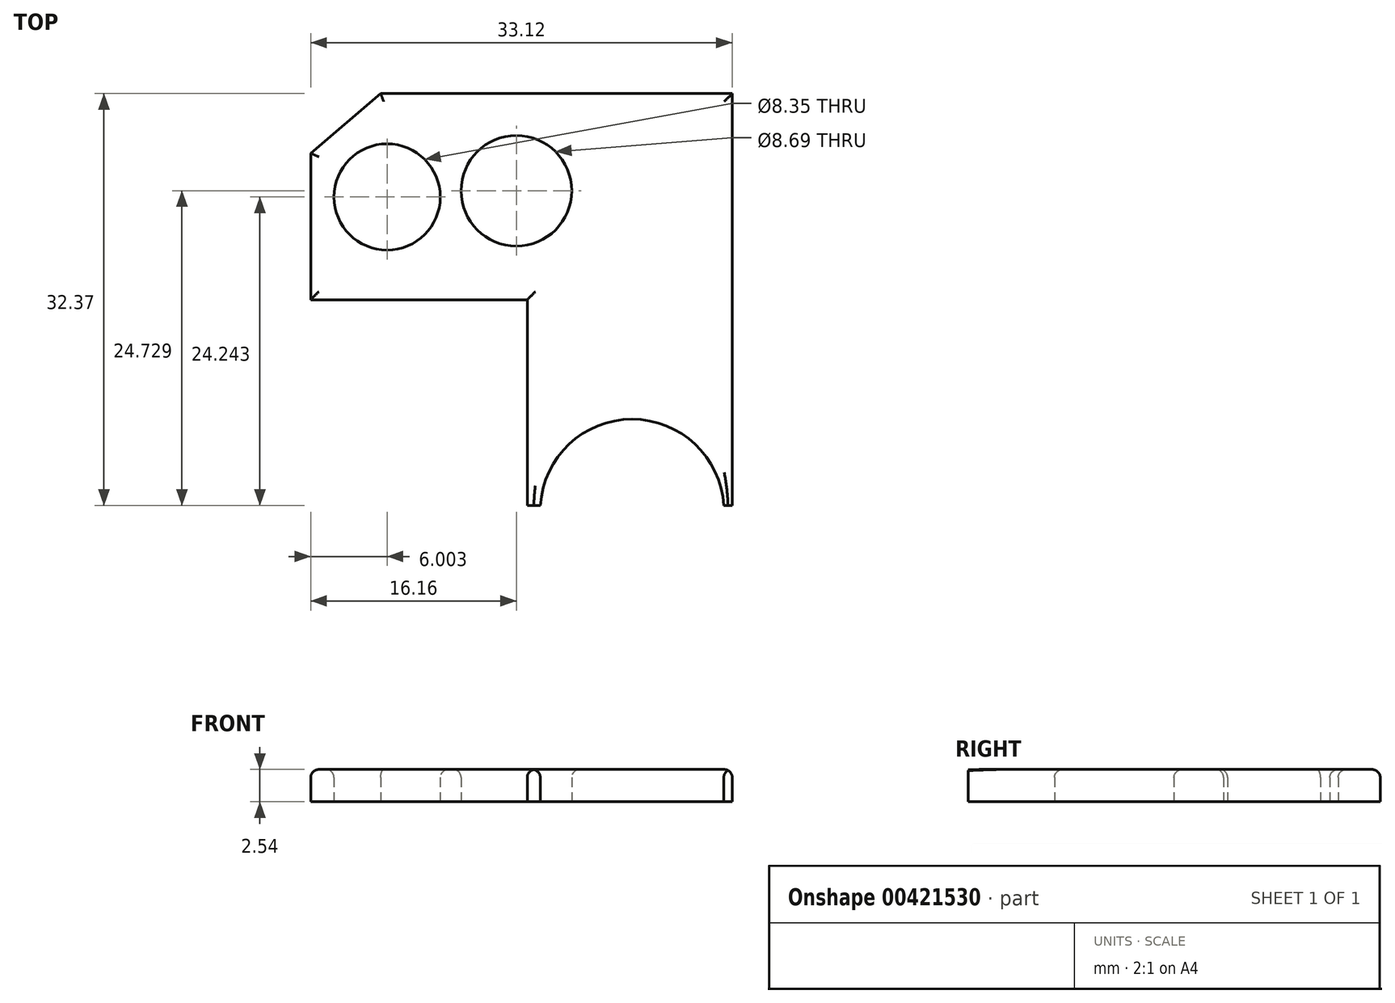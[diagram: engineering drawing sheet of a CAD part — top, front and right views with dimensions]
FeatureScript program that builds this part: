
annotation { "Feature Type Name" : "Feature", "Feature Type Description" : "" }
export const myFeature = defineFeature(function(context is Context, id is Id, definition is map)
    precondition{}
    {
        {
            var Q0;
            Q0=qCreatedBy(makeId("Top.planeOp"),FACE);
            var sketch = newSketch(context, id + "F0", { "sketchPlane" : qUnion([Q0])});
            skLineSegment(sketch, "E0", {"start": v(-16.16, 0) * mm, "end": v(-16.16, 7.98) * mm});
            skLineSegment(sketch, "E1", {"start": v(-16.16, 7.98) * mm, "end": v(-10.66, 12.67) * mm});
            skLineSegment(sketch, "E2", {"start": v(-10.66, 12.67) * mm, "end": v(16.96, 12.67) * mm});
            skLineSegment(sketch, "E3", {"start": v(16.96, 12.67) * mm, "end": v(16.96, 0) * mm});
            skLineSegment(sketch, "E4", {"start": v(16.96, 0) * mm, "end": v(16.96, -7) * mm});
            skLineSegment(sketch, "E5", {"start": v(16.96, -7) * mm, "end": v(0.86, -7) * mm});
            skLineSegment(sketch, "E6", {"start": v(0.86, -7) * mm, "end": v(0.86, -3.53) * mm});
            skLineSegment(sketch, "E7", {"start": v(0.86, -3.53) * mm, "end": v(-16.16, -3.53) * mm});
            skLineSegment(sketch, "E8", {"start": v(-16.16, -3.53) * mm, "end": v(-16.16, 0) * mm});
            skCircle(sketch, "E9", {"center": v(-10.16, 4.54) * mm, "radius": 4.18 * mm});
            skCircle(sketch, "E10", {"center": v(0, 5.03) * mm, "radius": 4.35 * mm});
            skSolve(sketch);
        }
        {
            var Q0;
            Q0=makeQuery(id+"F0.imprint","IMPRINT",FACE,{"disambiguationData":[TD([[makeQuery(id+"F0.imprint","IMPRINT",EDGE,{"derivedFrom":sQuery(id+"F0.wireOp",EDGE,"E0")}),-1.0]])]});
            extrude(context, id + "F1", {"entities" : qUnion([Q0]), "depth" : 2.54 * mm});
        }
        {
            var Q0;
            Q0=makeQuery(id+"F1.opExtrude","SWEPT_FACE",FACE,{"disambiguationData":[OSD([sQuery(id+"F0.wireOp",EDGE,"E5")])]});
            extrude(context, id + "F2", {"entities" : qUnion([Q0]), "operationType" : NewBodyOperationType.ADD, "depth" : 12.7 * mm});
        }
        {
            var Q0;
            Q0=qCreatedBy(makeId("Top.planeOp"),FACE);
            var sketch = newSketch(context, id + "F3", { "sketchPlane" : qUnion([Q0])});
            skCircle(sketch, "E11", {"center": v(6.55, -27.76) * mm, "radius": 7.22 * mm});
            skSolve(sketch);
        }
        {
            var Q0;
            Q0=makeQuery(id+"F3.imprint","IMPRINT",FACE,{"disambiguationData":[TD([[makeQuery(id+"F3.imprint","IMPRINT",EDGE,{"derivedFrom":sQuery(id+"F3.wireOp",EDGE,"E11")}),1.0]])]});
            extrude(context, id + "F4", {"entities" : qUnion([Q0]), "depth" : 12.7 * mm});
        }
        {
            var Q0;
            Q0=makeQuery(id+"F4.opExtrude","SWEPT_BODY",BODY,{"disambiguationData":[OSD([sQuery(id+"F3.wireOp",EDGE,"E11")])]});
            transform(context, id + "F5", {"entities" : qUnion([Q0]), "transformType" : TransformType.TRANSLATION_3D, "dx" : 2.54 * mm, "dy" : 7.62 * mm, "dz" : 0 * mm, "makeCopy" : false});
        }
        {
            var Q0;
            Q0=makeQuery(id+"F4.opExtrude","SWEPT_BODY",BODY,{"disambiguationData":[OSD([sQuery(id+"F3.wireOp",EDGE,"E11")])]});
            var Q1;
            Q1=makeQuery(id+"F1.opExtrude","SWEPT_BODY",BODY,{"disambiguationData":[OSD([sQuery(id+"F0.wireOp",EDGE,"E0"),sQuery(id+"F0.wireOp",EDGE,"E1"),sQuery(id+"F0.wireOp",EDGE,"E2"),sQuery(id+"F0.wireOp",EDGE,"E3"),sQuery(id+"F0.wireOp",EDGE,"E4"),sQuery(id+"F0.wireOp",EDGE,"E5"),sQuery(id+"F0.wireOp",EDGE,"E6"),sQuery(id+"F0.wireOp",EDGE,"E7"),sQuery(id+"F0.wireOp",EDGE,"E8"),sQuery(id+"F0.wireOp",EDGE,"E9"),sQuery(id+"F0.wireOp",EDGE,"E10")])]});
            booleanBodies(context, id + "F6", {"operationType" : BooleanOperationType.SUBTRACTION, "tools" : qUnion([Q0]), "targets" : qUnion([Q1])});
        }
        {
            var Q0;
            {var subQ0=sQuery(id+"F0.wireOp",EDGE,"E5");Q0=makeQuery(id+"F2.boolean.opBoolean","MERGE",FACE,{"derivedFrom":[makeQuery(id+"F1.opExtrude","CAP_FACE",FACE,{"disambiguationData":[OSD([sQuery(id+"F0.wireOp",EDGE,"E0"),sQuery(id+"F0.wireOp",EDGE,"E1"),sQuery(id+"F0.wireOp",EDGE,"E2"),sQuery(id+"F0.wireOp",EDGE,"E3"),sQuery(id+"F0.wireOp",EDGE,"E4"),subQ0,sQuery(id+"F0.wireOp",EDGE,"E6"),sQuery(id+"F0.wireOp",EDGE,"E7"),sQuery(id+"F0.wireOp",EDGE,"E8"),sQuery(id+"F0.wireOp",EDGE,"E9"),sQuery(id+"F0.wireOp",EDGE,"E10")])],"isStart":false}),makeQuery(id+"F2.opExtrude","SWEPT_FACE",FACE,{"disambiguationData":[OSD([subQ0]),TDD([makeQuery(id+"F1.opExtrude","CAP_EDGE",EDGE,{"disambiguationData":[OSD([subQ0])],"isStart":false})])]})]});}
            fillet(context, id + "F7", {"entities" : qUnion([Q0]), "radius" : 0.64 * mm, "tangentPropagation" : true, "allowEdgeOverflow" : false});
        }
    });
